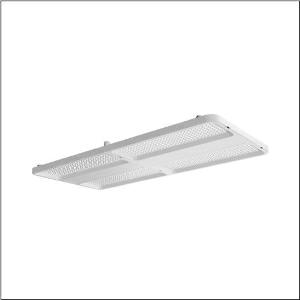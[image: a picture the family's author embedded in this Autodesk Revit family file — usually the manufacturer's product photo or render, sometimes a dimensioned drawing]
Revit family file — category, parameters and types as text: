
# Revit family: highbay_21_maxi_52hn12db4qea
name_source: partatom
category: Lighting Fixtures
units: mm (PartAtom-declared; Revit-internal decimal feet)

## family parameters
Cut with Voids When Loaded = No
Host = Face
Light Source = No
Part Type = Normal
Room Calculation Point = No
Round Connector Dimension = Use Diameter
Shared = No

## types (1)
- --- (1 x LED, 5840 lm, 31.4 W, 4000K)
    Apparent Load = 31 VA
    CIE Flux Codes = 90 98 100 100 100
    Color Rendering = 80
    Color Temperature = 4000K
    Default Elevation = 1800 mm
    Description = high bay luminaire Highbay 21 maxi; direct symmetric wide distribution, light control with lens of PMMA; UGR ≤ 22 (X = 4H | Y = 8H | S = 0.25H | reflection values 70/50/20); luminous flux: 38.000lm; light colour: 840, colour temperature: 4000K, MacAdam ≤ 3 SDCM (initial), colour rendering: CRI > 80; luminous efficacy: 192,2lm/W; rated service life: 75.000h (L80) at AT= ta max; control: DALI 2; luminaire connection: 2x terminal, 5-pole, max. 2.5mm² with through-wiring: 1x feed-in / 1x feed-out (cable entry for two cables, Ø 8.5..13mm); mains connection: 230..240V, AC/DC 0/50..60Hz; connected load: 197,7W; protection rating (complete): IP66; insulation class (complete): insulation class I (protective earthing); protection symbol: D; impact resistance: IK08; certification: CE, ENEC, VDE, UKCA; luminaire for central battery installations according to EN 60598-2-22, internal wiring halogen-free; luminaire LABS conformity tested according to VDMA 24364:2018-05; Suitable for use in the food industry according to the specifications of IFS-Food, HACCP and/or BRC; housing frame of high-performance plastic PA6, matt traffic white (RAL 9016); cover of PMMA; dimension (LxWxH): 946 x 442 x 72mm; permissible operating ambient temperature: -40..+60°C (reducing of maximum allowable ambient temperature of 5°C with ceiling mounting); packaging unit: 1 piece; (delivery without accessories; please order mounting accessories separately)
    Height = 72 mm  [stored 0.23622 ft]
    Lamp = 1 x LED
    Lamp Light Flux = 5840 lm
    Lamp Power = 31.4 W
    Lamp count = 1
    Length = 946 mm
    Luminous efficacy = 186 lm/W
    Manufacturer = Siteco
    ModVariant = No
    Model = 52HN12DB4QEA
    Mounting Place = Ceiling
    Mounting Type = Pendant
    Number of Poles = 1
    OnlyDefault = Yes
    Power Factor = 1
    Product Name = Highbay 21 maxi
    Product group = high bay luminaire
    ProductGroupID = 902
    Protection Class = Protection class I
    Protection Degree = IP 66
    RLX_Detail_Level = 1
    RLX_Emergency_Light_Flux = 0 lm
    RLX_Emergency_Type = 0
    RLX_Emergency_Type_DB = No
    RlxData = <blob elided: 128565 chars, md5=f94fd89d>
    Socket = socket
    Standby Power = 0 W
    System Light Flux = 5840 lm
    System Power = 31 W
    Type Comments = : DC mode (central or group accumulator) initial emergency light level
    Type Image = l_1363244.jpg
    URL = http://relux.com
    VarID = @adj_019277
    Voltage = 0 V
    Weight = 0.00 kg
    Width = 442 mm

note: [stored X ft] marks values corroborated as IEEE doubles in the binary element streams (Revit-internal decimal feet)

## geometry (parser evidence)
native form markers: Blend x4, Sweep x10
no freeform markers — native parametric forms only
